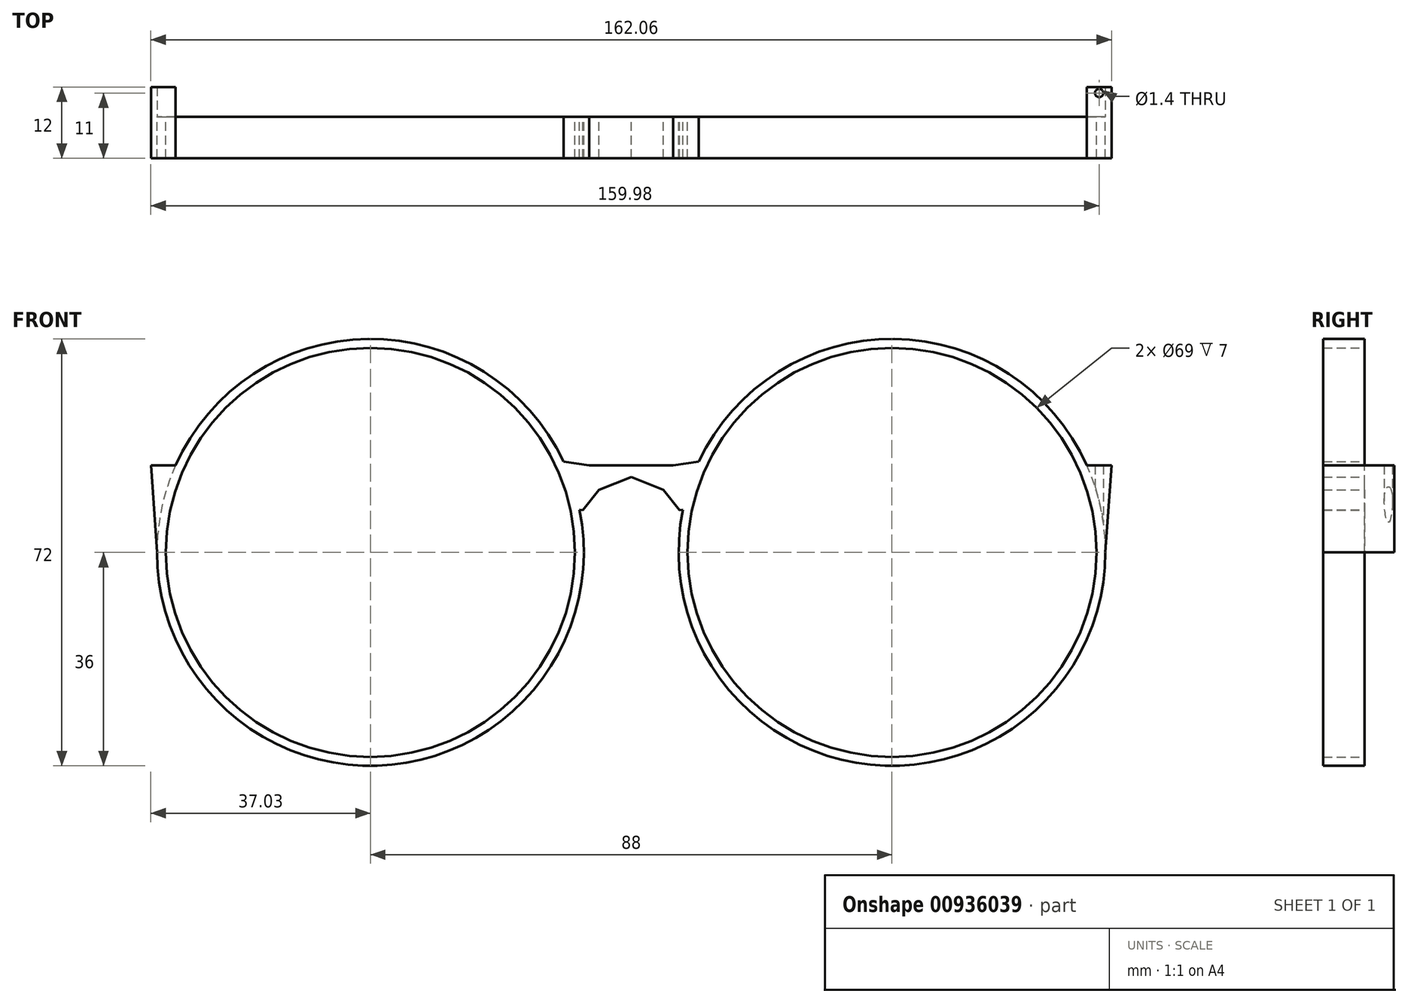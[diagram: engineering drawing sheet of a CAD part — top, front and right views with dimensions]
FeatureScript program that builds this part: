
annotation { "Feature Type Name" : "Feature", "Feature Type Description" : "" }
export const myFeature = defineFeature(function(context is Context, id is Id, definition is map)
    precondition{}
    {
        {
            var Q0;
            Q0=qCreatedBy(makeId("Front.planeOp"),FACE);
            var sketch = newSketch(context, id + "F0", { "sketchPlane" : qUnion([Q0])});
            skCircle(sketch, "E0", {"center": v(-44, 0) * mm, "radius": 34.5 * mm});
            skCircle(sketch, "E1", {"center": v(-44, 0) * mm, "radius": 36 * mm});
            skCircle(sketch, "E2.cCircle", {"center": v(-9.8, 11.22) * mm, "radius": 4.4 * mm, "construction": true});
            skLineSegment(sketch, "E2.0", {"start": v(-5.44, 10.58) * mm, "end": v(-8.17, 7.13) * mm});
            skLineSegment(sketch, "E2.1", {"start": v(-8.17, 7.13) * mm, "end": v(-12.52, 7.77) * mm});
            skLineSegment(sketch, "E2.2", {"start": v(-12.52, 7.77) * mm, "end": v(-14.15, 11.86) * mm});
            skLineSegment(sketch, "E2.3", {"start": v(-14.15, 11.86) * mm, "end": v(-11.42, 15.3) * mm});
            skLineSegment(sketch, "E2.4", {"start": v(-11.42, 15.3) * mm, "end": v(-7.06, 14.67) * mm});
            skLineSegment(sketch, "E2.5", {"start": v(-7.06, 14.67) * mm, "end": v(-5.44, 10.58) * mm});
            skLineSegment(sketch, "E3", {"start": v(-5.44, 10.58) * mm, "end": v(0, 12.74) * mm});
            skLineSegment(sketch, "E4", {"start": v(-7.06, 14.67) * mm, "end": v(0, 14.67) * mm});
            skLineSegment(sketch, "E5.MirrorCS", {"start": v(5.44, 10.58) * mm, "end": v(8.17, 7.13) * mm});
            skLineSegment(sketch, "E6.MirrorCS", {"start": v(8.17, 7.13) * mm, "end": v(12.52, 7.77) * mm});
            skLineSegment(sketch, "E7.MirrorCS", {"start": v(11.42, 15.3) * mm, "end": v(7.06, 14.67) * mm});
            skLineSegment(sketch, "E8.MirrorCS", {"start": v(14.15, 11.86) * mm, "end": v(11.42, 15.3) * mm});
            skLineSegment(sketch, "E9.MirrorCS", {"start": v(5.44, 10.58) * mm, "end": v(0, 12.74) * mm});
            skLineSegment(sketch, "E10.MirrorCS", {"start": v(12.52, 7.77) * mm, "end": v(14.15, 11.86) * mm});
            skLineSegment(sketch, "E11.MirrorCS", {"start": v(7.06, 14.67) * mm, "end": v(0, 14.67) * mm});
            skLineSegment(sketch, "E12.MirrorCS", {"start": v(7.06, 14.67) * mm, "end": v(5.44, 10.58) * mm});
            skCircle(sketch, "E13.MirrorC", {"center": v(44, 0) * mm, "radius": 34.5 * mm});
            skCircle(sketch, "E14.MirrorC", {"center": v(44, 0) * mm, "radius": 36 * mm});
            skCircle(sketch, "E15.MirrorC", {"center": v(9.8, 11.22) * mm, "radius": 4.4 * mm, "construction": true});
            skLineSegment(sketch, "E16", {"start": v(0, 14.67) * mm, "end": v(-76.87, 14.67) * mm, "construction": true});
            skLineSegment(sketch, "E17.top", {"start": v(-76.37, 14.67) * mm, "end": v(-81.03, 14.67) * mm});
            skLineSegment(sketch, "E17.right", {"start": v(-80, 0) * mm, "end": v(-81.03, 14.67) * mm});
            skLineSegment(sketch, "E18.MirrorCS", {"start": v(76.37, 14.67) * mm, "end": v(81.03, 14.67) * mm});
            skLineSegment(sketch, "E19.MirrorCS", {"start": v(80, 0) * mm, "end": v(81.03, 14.67) * mm});
            skLineSegment(sketch, "E20", {"start": v(80, 0) * mm, "end": v(80, 0) * mm});
            skLineSegment(sketch, "E21", {"start": v(-80, 0) * mm, "end": v(-80, 0) * mm});
            skSolve(sketch);
        }
        {
            var Q0;
            {var subQ0=sQuery(id+"F0.wireOp",EDGE,"E14.MirrorC");var subQ1=sQuery(id+"F0.wireOp",EDGE,"E6.MirrorCS");var subQ2=makeQuery(id+"F0.imprint","INTERSECT",VERTEX,{"derivedFrom":[subQ1,subQ0]});Q0=makeQuery(id+"F0.imprint","IMPRINT",FACE,{"disambiguationData":[TD([[makeQuery(id+"F0.imprint","IMPRINT",EDGE,{"disambiguationData":[TD([[subQ2,-1.0]])],"derivedFrom":subQ1}),-1.0]])]});}
            var Q1;
            {var subQ0=sQuery(id+"F0.wireOp",EDGE,"E2.1");var subQ1=sQuery(id+"F0.wireOp",EDGE,"E0");var subQ2=makeQuery(id+"F0.imprint","INTERSECT",VERTEX,{"derivedFrom":[subQ1,subQ0]});Q1=makeQuery(id+"F0.imprint","IMPRINT",FACE,{"disambiguationData":[TD([[makeQuery(id+"F0.imprint","IMPRINT",EDGE,{"disambiguationData":[TD([[subQ2,1.0]])],"derivedFrom":subQ1}),-1.0]])]});}
            var Q2;
            {var subQ0=sQuery(id+"F0.wireOp",EDGE,"E2.1");var subQ1=sQuery(id+"F0.wireOp",EDGE,"E0");var subQ2=makeQuery(id+"F0.imprint","INTERSECT",VERTEX,{"derivedFrom":[subQ1,subQ0]});Q2=makeQuery(id+"F0.imprint","IMPRINT",FACE,{"disambiguationData":[TD([[makeQuery(id+"F0.imprint","IMPRINT",EDGE,{"disambiguationData":[TD([[subQ2,-1.0]])],"derivedFrom":subQ1}),-1.0]])]});}
            var Q3;
            {var subQ5=sQuery(id+"F0.wireOp",EDGE,"E2.0");Q3=makeQuery(id+"F0.imprint","IMPRINT",FACE,{"disambiguationData":[TD([[makeQuery(id+"F0.imprint","IMPRINT",EDGE,{"derivedFrom":subQ5}),-1.0]])]});}
            var Q4;
            Q4=makeQuery(id+"F0.imprint","IMPRINT",FACE,{"disambiguationData":[TD([[makeQuery(id+"F0.imprint","IMPRINT",EDGE,{"derivedFrom":sQuery(id+"F0.wireOp",EDGE,"E2.5")}),1.0]])]});
            var Q5;
            {var subQ5=sQuery(id+"F0.wireOp",EDGE,"E5.MirrorCS");Q5=makeQuery(id+"F0.imprint","IMPRINT",FACE,{"disambiguationData":[TD([[makeQuery(id+"F0.imprint","IMPRINT",EDGE,{"derivedFrom":subQ5}),1.0]])]});}
            var Q6;
            {var subQ0=sQuery(id+"F0.wireOp",EDGE,"E14.MirrorC");var subQ1=sQuery(id+"F0.wireOp",EDGE,"E6.MirrorCS");var subQ2=makeQuery(id+"F0.imprint","INTERSECT",VERTEX,{"derivedFrom":[subQ1,subQ0]});Q6=makeQuery(id+"F0.imprint","IMPRINT",FACE,{"disambiguationData":[TD([[makeQuery(id+"F0.imprint","IMPRINT",EDGE,{"disambiguationData":[TD([[subQ2,-1.0]])],"derivedFrom":subQ1}),1.0]])]});}
            var Q7;
            {var subQ0=sQuery(id+"F0.wireOp",EDGE,"E18.MirrorCS");Q7=makeQuery(id+"F0.imprint","IMPRINT",FACE,{"disambiguationData":[TD([[makeQuery(id+"F0.imprint","IMPRINT",EDGE,{"derivedFrom":subQ0}),-1.0]])]});}
            var Q8;
            {var subQ0=sQuery(id+"F0.wireOp",EDGE,"E17.top");Q8=makeQuery(id+"F0.imprint","IMPRINT",FACE,{"disambiguationData":[TD([[makeQuery(id+"F0.imprint","IMPRINT",EDGE,{"derivedFrom":subQ0}),1.0]])]});}
            var Q9;
            {var subQ4=sQuery(id+"F0.wireOp",EDGE,"E17.bottom");Q9=makeQuery(id+"F0.imprint","IMPRINT",FACE,{"disambiguationData":[TD([[makeQuery(id+"F0.imprint","IMPRINT",EDGE,{"derivedFrom":subQ4}),-1.0]])]});}
            extrude(context, id + "F1", {"entities" : qUnion([Q0, Q1, Q2, Q3, Q4, Q5, Q6, Q7, Q8, Q9]), "depth" : 7 * mm, "offsetDistance" : 25 * mm});
        }
        {
            var Q0;
            {var subQ0=sQuery(id+"F0.wireOp",EDGE,"E17.top");Q0=makeQuery(id+"F0.imprint","IMPRINT",FACE,{"disambiguationData":[TD([[makeQuery(id+"F0.imprint","IMPRINT",EDGE,{"derivedFrom":subQ0}),1.0]])]});}
            var Q1;
            {var subQ0=sQuery(id+"F0.wireOp",EDGE,"E18.MirrorCS");Q1=makeQuery(id+"F0.imprint","IMPRINT",FACE,{"disambiguationData":[TD([[makeQuery(id+"F0.imprint","IMPRINT",EDGE,{"derivedFrom":subQ0}),-1.0]])]});}
            extrude(context, id + "F2", {"entities" : qUnion([Q0, Q1]), "operationType" : NewBodyOperationType.ADD, "oppositeDirection" : true, "depth" : 5 * mm, "offsetDistance" : 25 * mm});
        }
        {
            var Q0;
            Q0=qCreatedBy(makeId("Top.planeOp"),FACE);
            var sketch = newSketch(context, id + "F3", { "sketchPlane" : qUnion([Q0])});
            skLineSegment(sketch, "E22", {"start": v(78.95, 5) * mm, "end": v(78.95, -10.9) * mm, "construction": true});
            skLineSegment(sketch, "E23", {"start": v(76.87, 4) * mm, "end": v(81.03, 4) * mm, "construction": true});
            skCircle(sketch, "E24", {"center": v(78.95, 4) * mm, "radius": 0.7 * mm});
            skCircle(sketch, "E25.MirrorC", {"center": v(-78.95, 4) * mm, "radius": 0.7 * mm});
            skSolve(sketch);
        }
        {
            var Q0;
            Q0=makeQuery(id+"F3.imprint","IMPRINT",FACE,{"disambiguationData":[TD([[makeQuery(id+"F3.imprint","IMPRINT",EDGE,{"derivedFrom":sQuery(id+"F3.wireOp",EDGE,"E25.MirrorC")}),-1.0]])]});
            var Q1;
            Q1=makeQuery(id+"F3.imprint","IMPRINT",FACE,{"disambiguationData":[TD([[makeQuery(id+"F3.imprint","IMPRINT",EDGE,{"derivedFrom":sQuery(id+"F3.wireOp",EDGE,"E24")}),1.0]])]});
            extrude(context, id + "F4", {"entities" : qUnion([Q0, Q1]), "operationType" : NewBodyOperationType.REMOVE, "endBound" : BoundingType.THROUGH_ALL, "depth" : 25 * mm, "offsetDistance" : 25 * mm});
        }
    });
